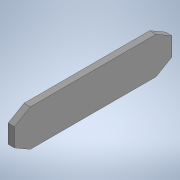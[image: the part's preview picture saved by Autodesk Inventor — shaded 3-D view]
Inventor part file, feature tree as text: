
AUTODESK INVENTOR PART (.ipt)
format: ipt  version: 2020 (Build 240168000, 168)  size: 109,568 bytes
history: native  units: in
note: dims shown in document units (in); Inventor stores cm internally (conversion verified against a paired STEP export)
features: extrude x1, sketch x1
ambient origin geometry x8: Origin, YZ Plane, XZ Plane, XY Plane, X Axis, Y Axis, Z Axis, Center Point
bodies: Solid1 (feature_tree)
feature tree (2):
  extrude  "Extrusion1"  Depth=5.9055in
  sketch  "Sketch1"  dims[d0=1.378in d1=5.9055in d2=0.2362in d3=0.0in]
